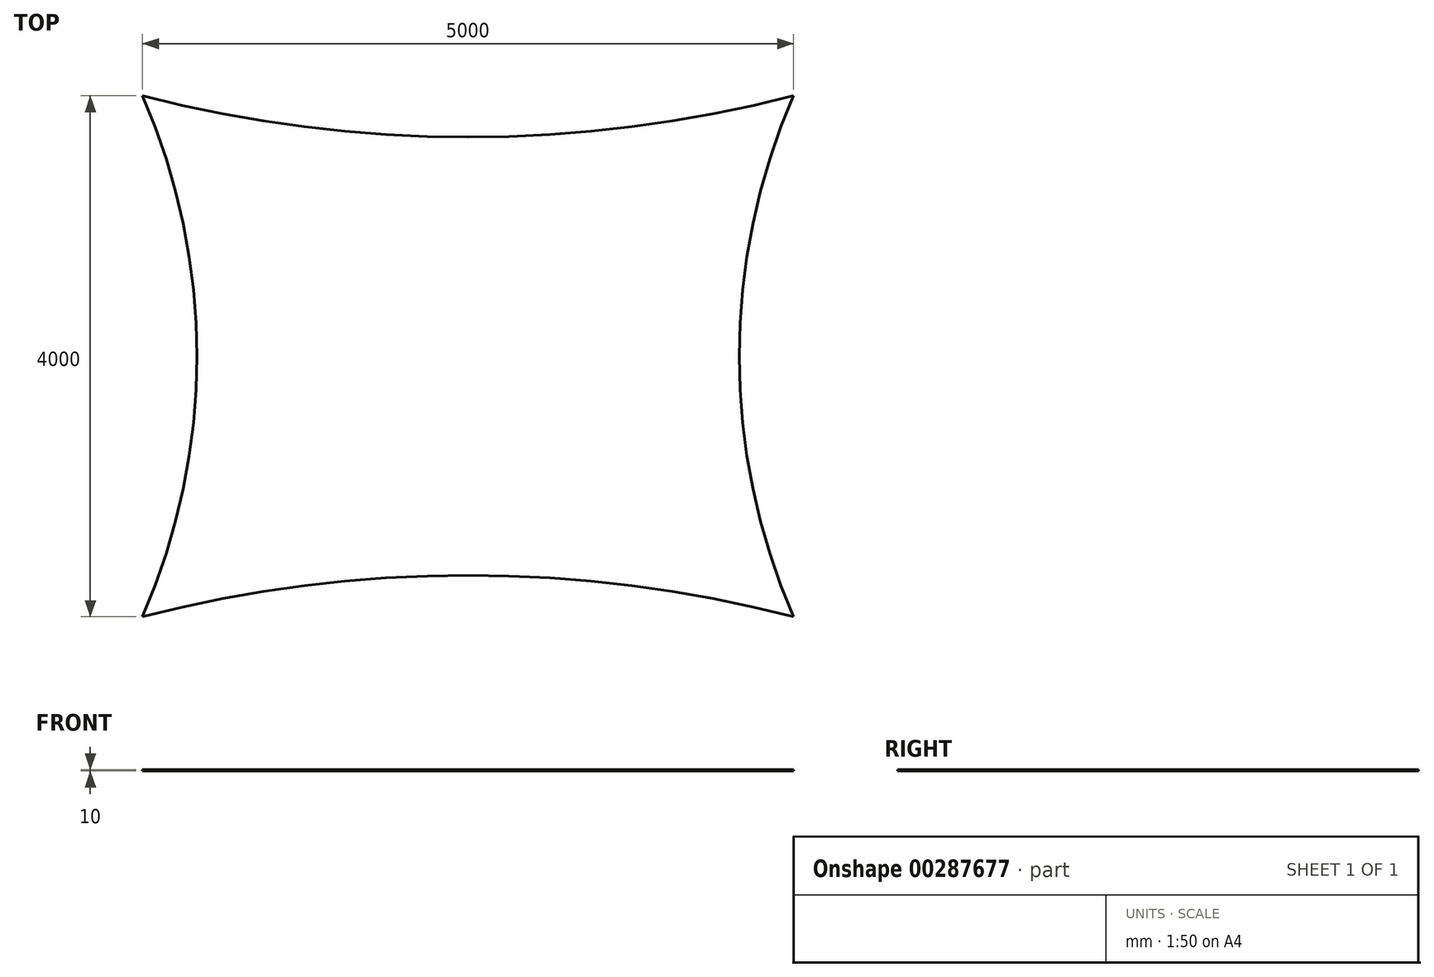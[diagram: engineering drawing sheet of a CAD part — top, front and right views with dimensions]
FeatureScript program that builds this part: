
annotation { "Feature Type Name" : "Feature", "Feature Type Description" : "" }
export const myFeature = defineFeature(function(context is Context, id is Id, definition is map)
    precondition{}
    {
        {
            var Q0;
            Q0=qCreatedBy(makeId("Top.planeOp"),FACE);
            var sketch = newSketch(context, id + "F0", { "sketchPlane" : qUnion([Q0])});
            skLineSegment(sketch, "E0.bottom", {"start": v(2500, 2000) * mm, "end": v(-2500, 2000) * mm, "construction": true});
            skLineSegment(sketch, "E0.top", {"start": v(2500, -2000) * mm, "end": v(-2500, -2000) * mm, "construction": true});
            skLineSegment(sketch, "E0.left", {"start": v(2500, 2000) * mm, "end": v(2500, -2000) * mm, "construction": true});
            skLineSegment(sketch, "E0.right", {"start": v(-2500, 2000) * mm, "end": v(-2500, -2000) * mm, "construction": true});
            skPoint(sketch, "E0.middle", {"position": v(0, 0) * mm});
            skArc(sketch, "E1", {"start": v(-2500, 2000) * mm, "mid": v(0, 1682.46) * mm, "end": v(2500, 2000) * mm});
            skArc(sketch, "E2", {"start": v(2500, -2000) * mm, "mid": v(0, -1682.46) * mm, "end": v(-2500, -2000) * mm});
            skArc(sketch, "E3", {"start": v(2500, 2000) * mm, "mid": v(2082.58, 0) * mm, "end": v(2500, -2000) * mm});
            skArc(sketch, "E4", {"start": v(-2500, -2000) * mm, "mid": v(-2082.58, 0) * mm, "end": v(-2500, 2000) * mm});
            skSolve(sketch);
        }
        {
            var Q0;
            Q0=makeQuery(id+"F0.imprint","IMPRINT",FACE,{"disambiguationData":[TD([[makeQuery(id+"F0.imprint","IMPRINT",EDGE,{"derivedFrom":sQuery(id+"F0.wireOp",EDGE,"E1")}),-1.0]])]});
            extrude(context, id + "F1", {"entities" : qUnion([Q0]), "depth" : 10 * mm, "offsetDistance" : 25 * mm});
        }
    });
